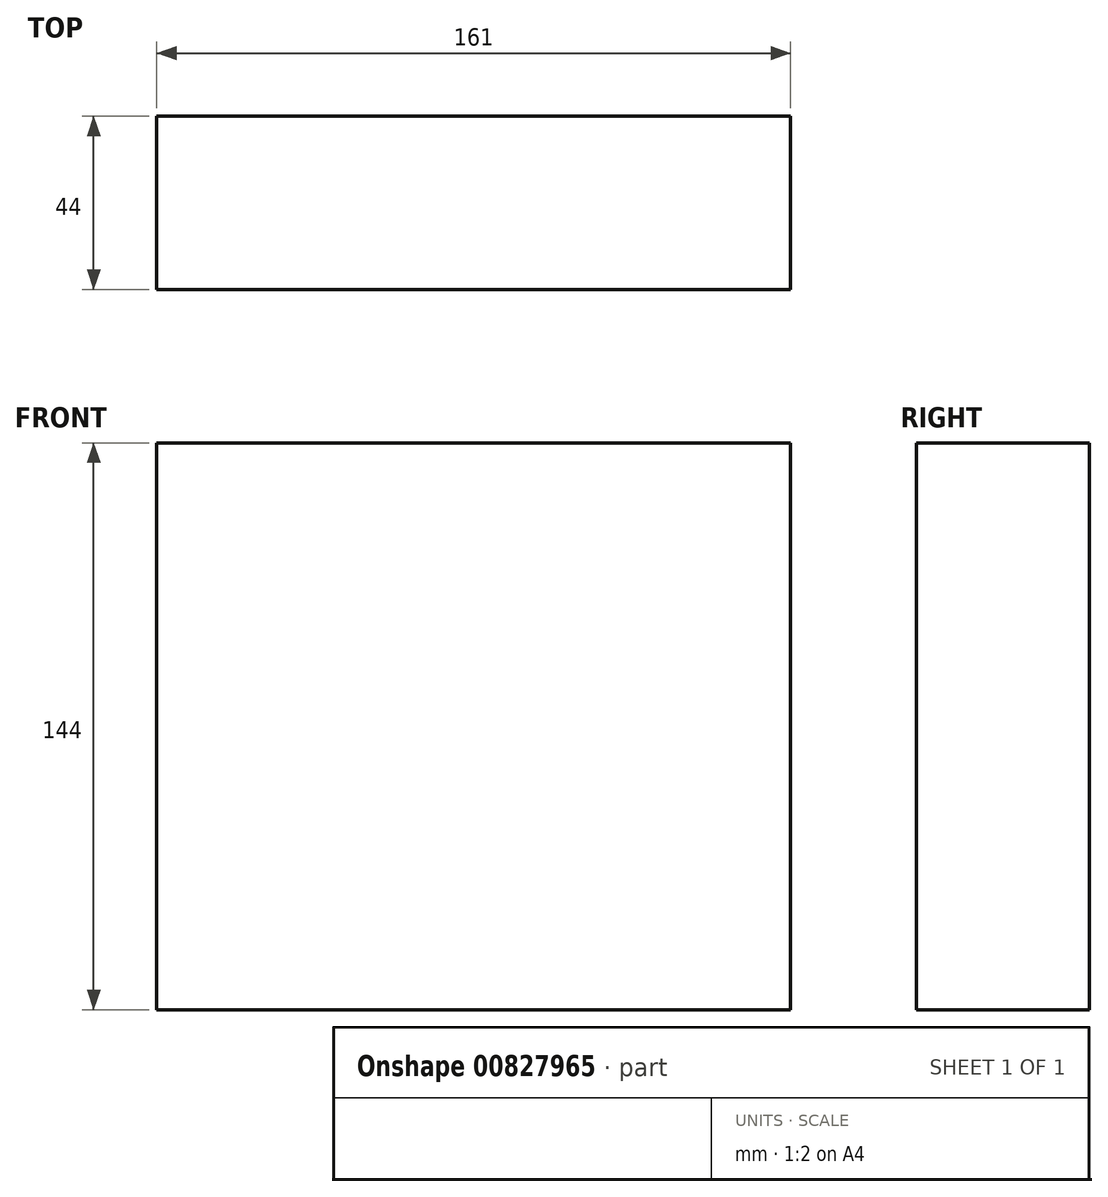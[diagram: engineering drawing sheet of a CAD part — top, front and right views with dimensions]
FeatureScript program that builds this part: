
annotation { "Feature Type Name" : "Feature", "Feature Type Description" : "" }
export const myFeature = defineFeature(function(context is Context, id is Id, definition is map)
    precondition{}
    {
        {
            var Q0;
            Q0=qCreatedBy(makeId("Top.planeOp"),FACE);
            var sketch = newSketch(context, id + "F0", { "sketchPlane" : qUnion([Q0])});
            skLineSegment(sketch, "E0.bottom", {"start": v(-80.5, 22) * mm, "end": v(80.5, 22) * mm});
            skLineSegment(sketch, "E0.top", {"start": v(-80.5, -22) * mm, "end": v(80.5, -22) * mm});
            skLineSegment(sketch, "E0.left", {"start": v(-80.5, 22) * mm, "end": v(-80.5, -22) * mm});
            skLineSegment(sketch, "E0.right", {"start": v(80.5, 22) * mm, "end": v(80.5, -22) * mm});
            skPoint(sketch, "E0.middle", {"position": v(0, 0) * mm});
            skSolve(sketch);
        }
        {
            var Q0;
            Q0=makeQuery(id+"F0.imprint","IMPRINT",FACE,{"disambiguationData":[TD([[makeQuery(id+"F0.imprint","IMPRINT",EDGE,{"derivedFrom":sQuery(id+"F0.wireOp",EDGE,"E0.bottom")}),-1.0]])]});
            extrude(context, id + "F1", {"entities" : qUnion([Q0]), "depth" : 144 * mm, "offsetDistance" : 25 * mm});
        }
    });
